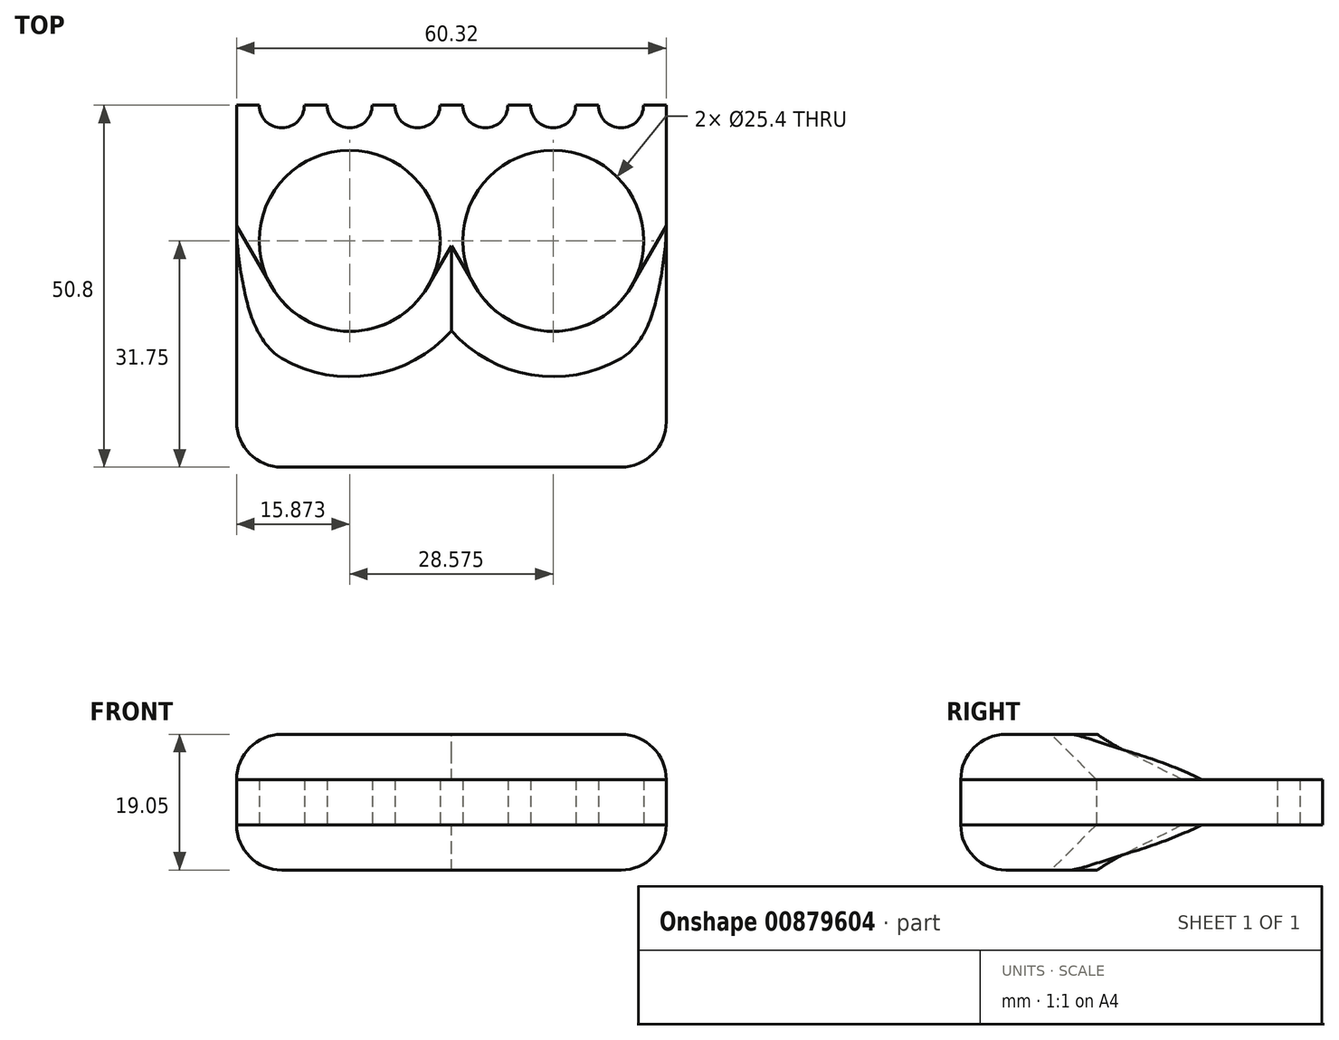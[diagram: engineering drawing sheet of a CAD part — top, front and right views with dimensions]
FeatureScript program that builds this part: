
annotation { "Feature Type Name" : "Feature", "Feature Type Description" : "" }
export const myFeature = defineFeature(function(context is Context, id is Id, definition is map)
    precondition{}
    {
        {
            var Q0;
            Q0=qCreatedBy(makeId("Top.planeOp"),FACE);
            var sketch = newSketch(context, id + "F0", { "sketchPlane" : qUnion([Q0])});
            skLineSegment(sketch, "E0.bottom", {"start": v(23.81, -25.4) * mm, "end": v(-23.81, -25.4) * mm});
            skLineSegment(sketch, "E0.top", {"start": v(30.16, 25.4) * mm, "end": v(-30.16, 25.4) * mm});
            skLineSegment(sketch, "E0.left", {"start": v(30.16, -19.05) * mm, "end": v(30.16, 25.4) * mm});
            skLineSegment(sketch, "E0.right", {"start": v(-30.16, -19.05) * mm, "end": v(-30.16, 25.4) * mm});
            skPoint(sketch, "E0.middle", {"position": v(0, 0) * mm});
            skCircle(sketch, "E1", {"center": v(14.29, 6.35) * mm, "radius": 12.7 * mm});
            skCircle(sketch, "E2", {"center": v(-14.29, 6.35) * mm, "radius": 12.7 * mm});
            skPoint(sketch, "E3.visualSharp", {"position": v(-30.16, -25.4) * mm});
            skArc(sketch, "E3.filletArc", {"start": v(-30.16, -19.05) * mm, "mid": v(-28.3, -23.54) * mm, "end": v(-23.81, -25.4) * mm});
            skPoint(sketch, "E4.visualSharp", {"position": v(30.16, -25.4) * mm});
            skArc(sketch, "E4.filletArc", {"start": v(23.81, -25.4) * mm, "mid": v(28.3, -23.54) * mm, "end": v(30.16, -19.05) * mm});
            skLineSegment(sketch, "E5", {"start": v(-30.16, 22.23) * mm, "end": v(30.16, 22.23) * mm, "construction": true});
            skArc(sketch, "E6", {"start": v(-26.99, 25.4) * mm, "mid": v(-23.81, 22.23) * mm, "end": v(-20.64, 25.4) * mm});
            skArc(sketch, "E7", {"start": v(26.99, 25.4) * mm, "mid": v(23.81, 22.23) * mm, "end": v(20.64, 25.4) * mm});
            skArc(sketch, "E8", {"start": v(17.46, 25.4) * mm, "mid": v(14.29, 22.23) * mm, "end": v(11.11, 25.4) * mm});
            skArc(sketch, "E9", {"start": v(-17.46, 25.4) * mm, "mid": v(-14.29, 22.23) * mm, "end": v(-11.11, 25.4) * mm});
            skArc(sketch, "E10", {"start": v(-7.94, 25.4) * mm, "mid": v(-4.76, 22.23) * mm, "end": v(-1.59, 25.4) * mm});
            skArc(sketch, "E11", {"start": v(7.94, 25.4) * mm, "mid": v(4.76, 22.23) * mm, "end": v(1.59, 25.4) * mm});
            skSolve(sketch);
        }
        {
            var Q0;
            Q0=makeQuery(id+"F0.imprint","IMPRINT",FACE,{"disambiguationData":[TD([[makeQuery(id+"F0.imprint","IMPRINT",EDGE,{"derivedFrom":sQuery(id+"F0.wireOp",EDGE,"E0.bottom")}),-1.0]])]});
            extrude(context, id + "F1", {"entities" : qUnion([Q0]), "depth" : 6.35 * mm, "offsetDistance" : 25.4 * mm});
        }
        {
            var Q0;
            Q0=qCreatedBy(makeId("Top.planeOp"),FACE);
            var sketch = newSketch(context, id + "F2", { "sketchPlane" : qUnion([Q0])});
            skLineSegment(sketch, "E12.bottom", {"start": v(30.16, 0) * mm, "end": v(25.29, 0) * mm, "construction": true});
            skLineSegment(sketch, "E12.top", {"start": v(23.81, -25.4) * mm, "end": v(-23.81, -25.4) * mm});
            skLineSegment(sketch, "E12.left", {"start": v(30.16, 0) * mm, "end": v(30.16, -19.05) * mm});
            skLineSegment(sketch, "E12.right", {"start": v(-30.16, 0) * mm, "end": v(-30.16, -19.05) * mm});
            skPoint(sketch, "E12.middle", {"position": v(0, -12.7) * mm});
            skArc(sketch, "E13", {"start": v(25.29, 0) * mm, "mid": v(14.29, -6.35) * mm, "end": v(3.29, 0) * mm});
            skArc(sketch, "E14", {"start": v(-25.29, 0) * mm, "mid": v(-14.29, -6.35) * mm, "end": v(-3.29, 0) * mm});
            skLineSegment(sketch, "E15.trimOffspring", {"start": v(-25.29, 0) * mm, "end": v(-30.16, 0) * mm, "construction": true});
            skLineSegment(sketch, "E16.trimOffspring", {"start": v(3.29, 0) * mm, "end": v(-3.29, 0) * mm, "construction": true});
            skPoint(sketch, "E17.visualSharp", {"position": v(30.16, -25.4) * mm});
            skArc(sketch, "E17.filletArc", {"start": v(23.81, -25.4) * mm, "mid": v(28.3, -23.54) * mm, "end": v(30.16, -19.05) * mm});
            skPoint(sketch, "E18.visualSharp", {"position": v(-30.16, -25.4) * mm});
            skArc(sketch, "E18.filletArc", {"start": v(-30.16, -19.05) * mm, "mid": v(-28.3, -23.54) * mm, "end": v(-23.81, -25.4) * mm});
            skLineSegment(sketch, "E19", {"start": v(3.29, 0) * mm, "end": v(0, 5.7) * mm});
            skLineSegment(sketch, "E20", {"start": v(0, 5.7) * mm, "end": v(-3.29, 0) * mm});
            skLineSegment(sketch, "E21", {"start": v(25.29, 0) * mm, "end": v(30.16, 8.45) * mm});
            skLineSegment(sketch, "E22", {"start": v(30.16, 8.45) * mm, "end": v(30.16, 0) * mm});
            skLineSegment(sketch, "E23", {"start": v(-25.29, 0) * mm, "end": v(-30.16, 8.45) * mm});
            skLineSegment(sketch, "E24", {"start": v(-30.16, 8.45) * mm, "end": v(-30.16, 0) * mm});
            skSolve(sketch);
        }
        {
            var Q0;
            Q0 = qSketchRegion(id + "F2", true);
            extrude(context, id + "F3", {"entities" : qUnion([Q0]), "depth" : 12.7 * mm, "offsetDistance" : 25.4 * mm, "hasSecondDirection" : true, "secondDirectionOppositeDirection" : false, "secondDirectionDepth" : 6.35 * mm});
        }
        {
            var Q0;
            Q0 = qSketchRegion(id + "F2", true);
            extrude(context, id + "F4", {"entities" : qUnion([Q0]), "oppositeDirection" : true, "depth" : 6.35 * mm, "offsetDistance" : 25.4 * mm});
        }
        {
            var Q0;
            Q0=makeQuery(id+"F3.opExtrude","CAP_EDGE",EDGE,{"disambiguationData":[OSD([sQuery(id+"F2.wireOp",EDGE,"E14")])],"isStart":false});
            var Q1;
            Q1=makeQuery(id+"F3.opExtrude","CAP_EDGE",EDGE,{"disambiguationData":[OSD([sQuery(id+"F2.wireOp",EDGE,"E13")])],"isStart":false});
            var Q2;
            Q2=makeQuery(id+"F4.opExtrude","CAP_EDGE",EDGE,{"disambiguationData":[OSD([sQuery(id+"F2.wireOp",EDGE,"E13")])],"isStart":false});
            var Q3;
            Q3=makeQuery(id+"F4.opExtrude","CAP_EDGE",EDGE,{"disambiguationData":[OSD([sQuery(id+"F2.wireOp",EDGE,"E14")])],"isStart":false});
            chamfer(context, id + "F5", {"entities" : qUnion([Q0, Q1, Q2, Q3]), "width" : 6.35 * mm, "tangentPropagation" : true});
        }
        {
            var Q0;
            Q0=makeQuery(id+"F3.opExtrude","CAP_EDGE",EDGE,{"disambiguationData":[OSD([sQuery(id+"F2.wireOp",EDGE,"E12.top")])],"isStart":false});
            var Q1;
            Q1=makeQuery(id+"F3.opExtrude","CAP_EDGE",EDGE,{"disambiguationData":[OSD([sQuery(id+"F2.wireOp",EDGE,"E18.filletArc")])],"isStart":false});
            var Q2;
            Q2=makeQuery(id+"F3.opExtrude","CAP_EDGE",EDGE,{"disambiguationData":[OSD([sQuery(id+"F2.wireOp",EDGE,"E12.right")])],"isStart":false});
            var Q3;
            Q3=makeQuery(id+"F3.opExtrude","CAP_EDGE",EDGE,{"disambiguationData":[OSD([sQuery(id+"F2.wireOp",EDGE,"E17.filletArc")])],"isStart":false});
            var Q4;
            Q4=makeQuery(id+"F3.opExtrude","CAP_EDGE",EDGE,{"disambiguationData":[OSD([sQuery(id+"F2.wireOp",EDGE,"E12.left")])],"isStart":false});
            var Q5;
            Q5=makeQuery(id+"F4.opExtrude","CAP_EDGE",EDGE,{"disambiguationData":[OSD([sQuery(id+"F2.wireOp",EDGE,"E12.left")])],"isStart":false});
            var Q6;
            Q6=makeQuery(id+"F4.opExtrude","CAP_EDGE",EDGE,{"disambiguationData":[OSD([sQuery(id+"F2.wireOp",EDGE,"E17.filletArc")])],"isStart":false});
            var Q7;
            Q7=makeQuery(id+"F4.opExtrude","CAP_EDGE",EDGE,{"disambiguationData":[OSD([sQuery(id+"F2.wireOp",EDGE,"E12.top")])],"isStart":false});
            var Q8;
            Q8=makeQuery(id+"F4.opExtrude","CAP_EDGE",EDGE,{"disambiguationData":[OSD([sQuery(id+"F2.wireOp",EDGE,"E18.filletArc")])],"isStart":false});
            var Q9;
            Q9=makeQuery(id+"F4.opExtrude","CAP_EDGE",EDGE,{"disambiguationData":[OSD([sQuery(id+"F2.wireOp",EDGE,"E12.right")])],"isStart":false});
            fillet(context, id + "F6", {"entities" : qUnion([Q0, Q1, Q2, Q3, Q4, Q5, Q6, Q7, Q8, Q9]), "radius" : 6.35 * mm, "tangentPropagation" : true, "allowEdgeOverflow" : false});
        }
    });
